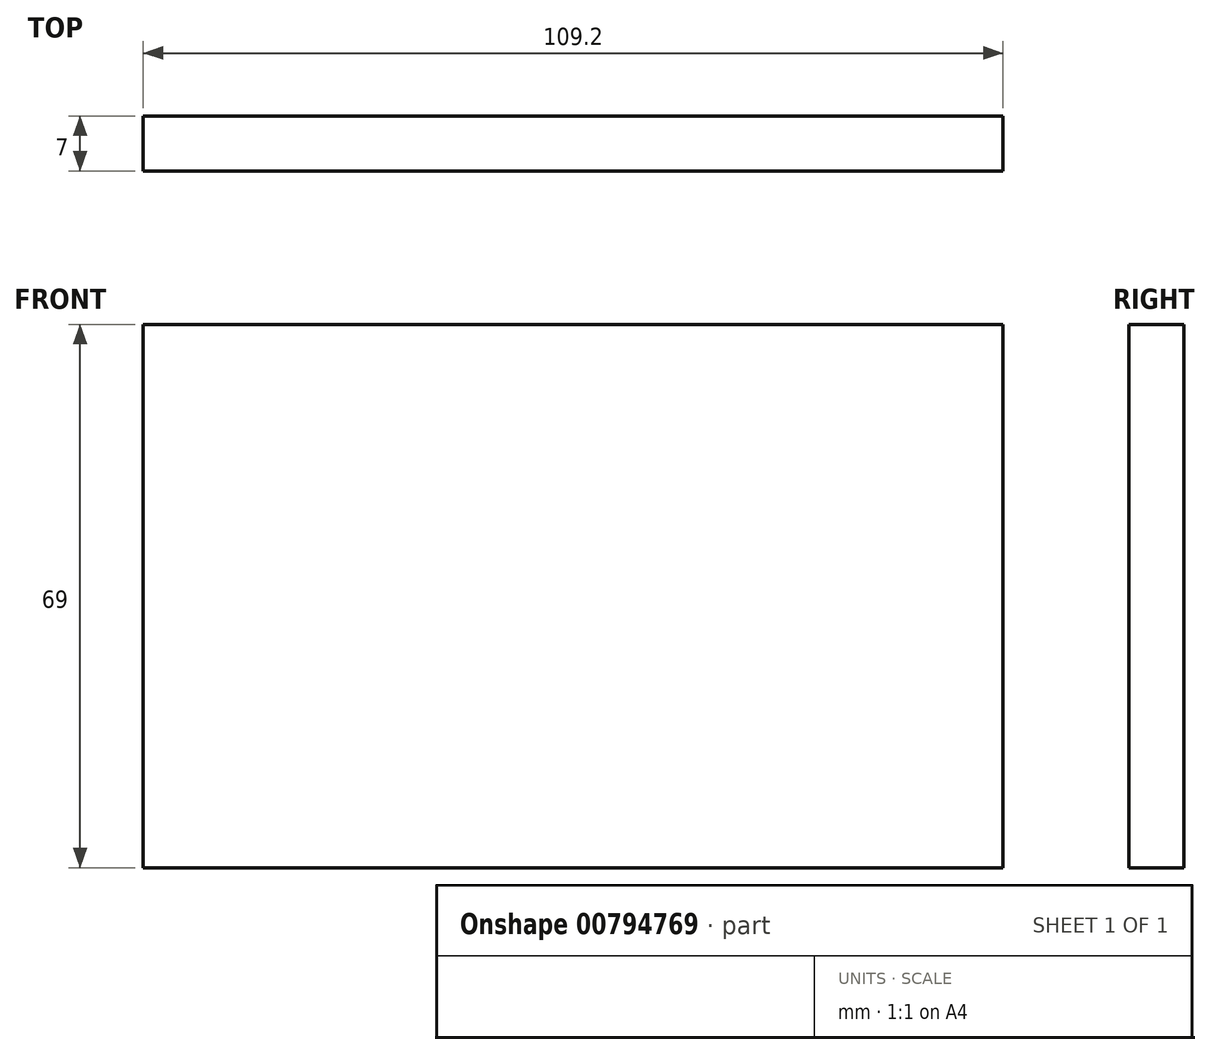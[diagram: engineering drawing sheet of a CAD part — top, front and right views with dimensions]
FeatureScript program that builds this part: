
annotation { "Feature Type Name" : "Feature", "Feature Type Description" : "" }
export const myFeature = defineFeature(function(context is Context, id is Id, definition is map)
    precondition{}
    {
        {
            var Q0;
            Q0=qCreatedBy(makeId("Front.planeOp"),FACE);
            var sketch = newSketch(context, id + "F0", { "sketchPlane" : qUnion([Q0])});
            skLineSegment(sketch, "E0.bottom", {"start": v(54.6, -34.5) * mm, "end": v(-54.6, -34.5) * mm});
            skLineSegment(sketch, "E0.top", {"start": v(54.6, 34.5) * mm, "end": v(-54.6, 34.5) * mm});
            skLineSegment(sketch, "E0.left", {"start": v(54.6, -34.5) * mm, "end": v(54.6, 34.5) * mm});
            skLineSegment(sketch, "E0.right", {"start": v(-54.6, -34.5) * mm, "end": v(-54.6, 34.5) * mm});
            skPoint(sketch, "E0.middle", {"position": v(0, 0) * mm});
            skSolve(sketch);
        }
        {
            var Q0;
            Q0=makeQuery(id+"F0.imprint","IMPRINT",FACE,{"disambiguationData":[TD([[makeQuery(id+"F0.imprint","IMPRINT",EDGE,{"derivedFrom":sQuery(id+"F0.wireOp",EDGE,"E0.bottom")}),-1.0]])]});
            extrude(context, id + "F1", {"entities" : qUnion([Q0]), "depth" : 7 * mm, "offsetDistance" : 25 * mm});
        }
    });
